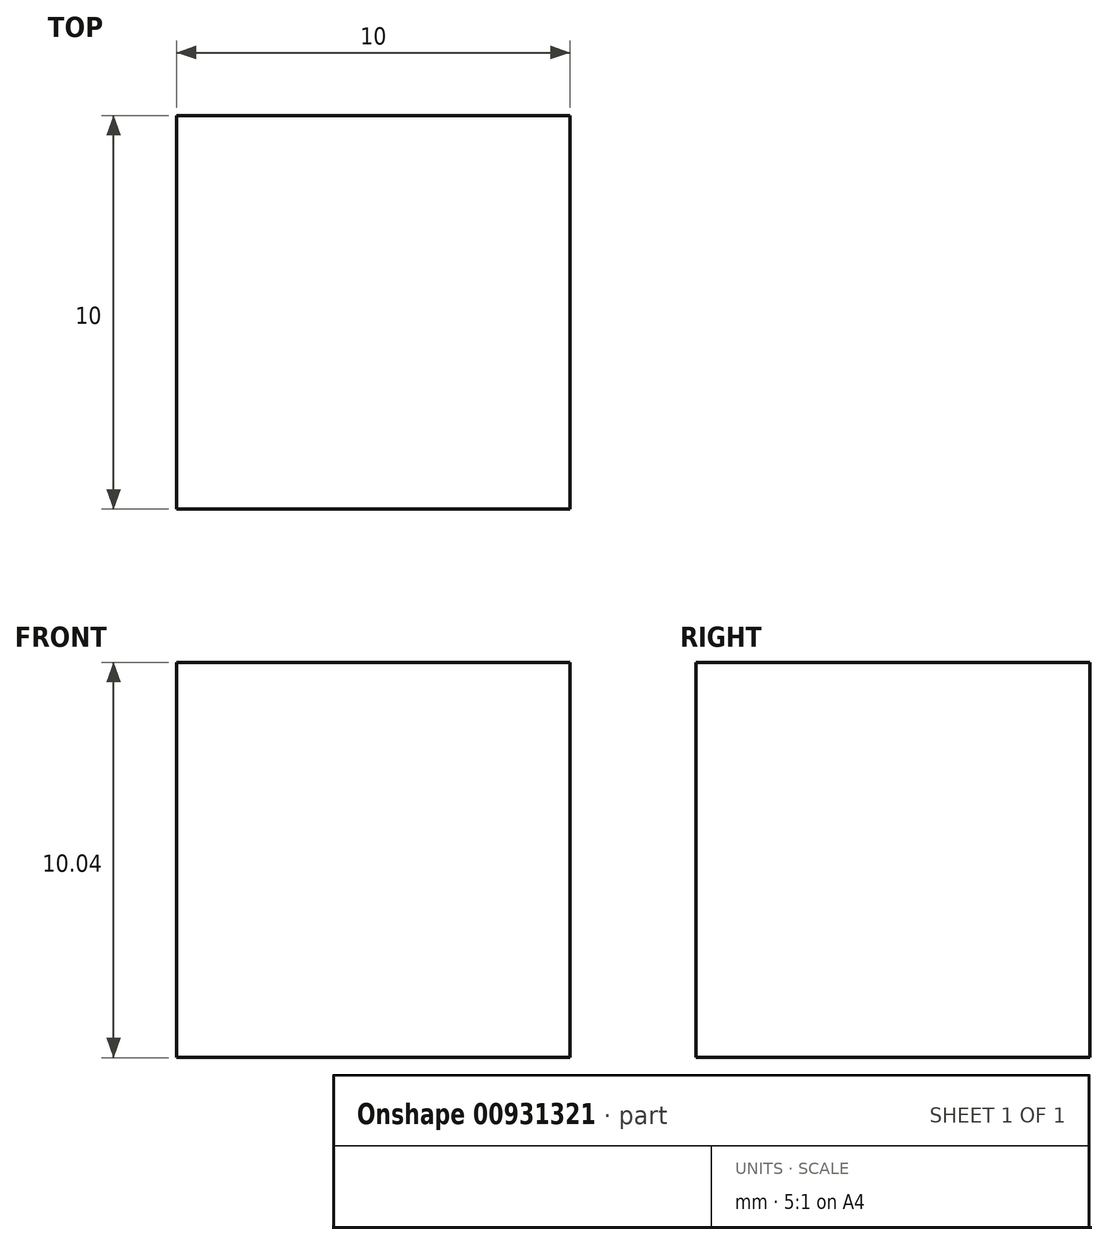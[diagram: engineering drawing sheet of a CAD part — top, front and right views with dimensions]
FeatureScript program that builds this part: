
annotation { "Feature Type Name" : "Feature", "Feature Type Description" : "" }
export const myFeature = defineFeature(function(context is Context, id is Id, definition is map)
    precondition{}
    {
        {
            var Q0;
            Q0=qCreatedBy(makeId("Front.planeOp"),FACE);
            var sketch = newSketch(context, id + "F0", { "sketchPlane" : qUnion([Q0])});
            skPoint(sketch, "E0.middle", {"position": v(0, 0) * mm});
            skLineSegment(sketch, "E1.bottom", {"start": v(-5, -5.02) * mm, "end": v(5, -5.02) * mm});
            skLineSegment(sketch, "E1.top", {"start": v(-5, 5.02) * mm, "end": v(5, 5.02) * mm});
            skLineSegment(sketch, "E1.left", {"start": v(-5, -5.02) * mm, "end": v(-5, 5.02) * mm});
            skLineSegment(sketch, "E1.right", {"start": v(5, -5.02) * mm, "end": v(5, 5.02) * mm});
            skSolve(sketch);
        }
        {
            var Q0;
            Q0=makeQuery(id+"F0.imprint","IMPRINT",FACE,{"disambiguationData":[TD([[makeQuery(id+"F0.imprint","IMPRINT",EDGE,{"derivedFrom":sQuery(id+"F0.wireOp",EDGE,"E1.bottom")}),1.0]])]});
            extrude(context, id + "F1", {"entities" : qUnion([Q0]), "depth" : 10 * mm, "offsetDistance" : 25.4 * mm});
        }
    });
